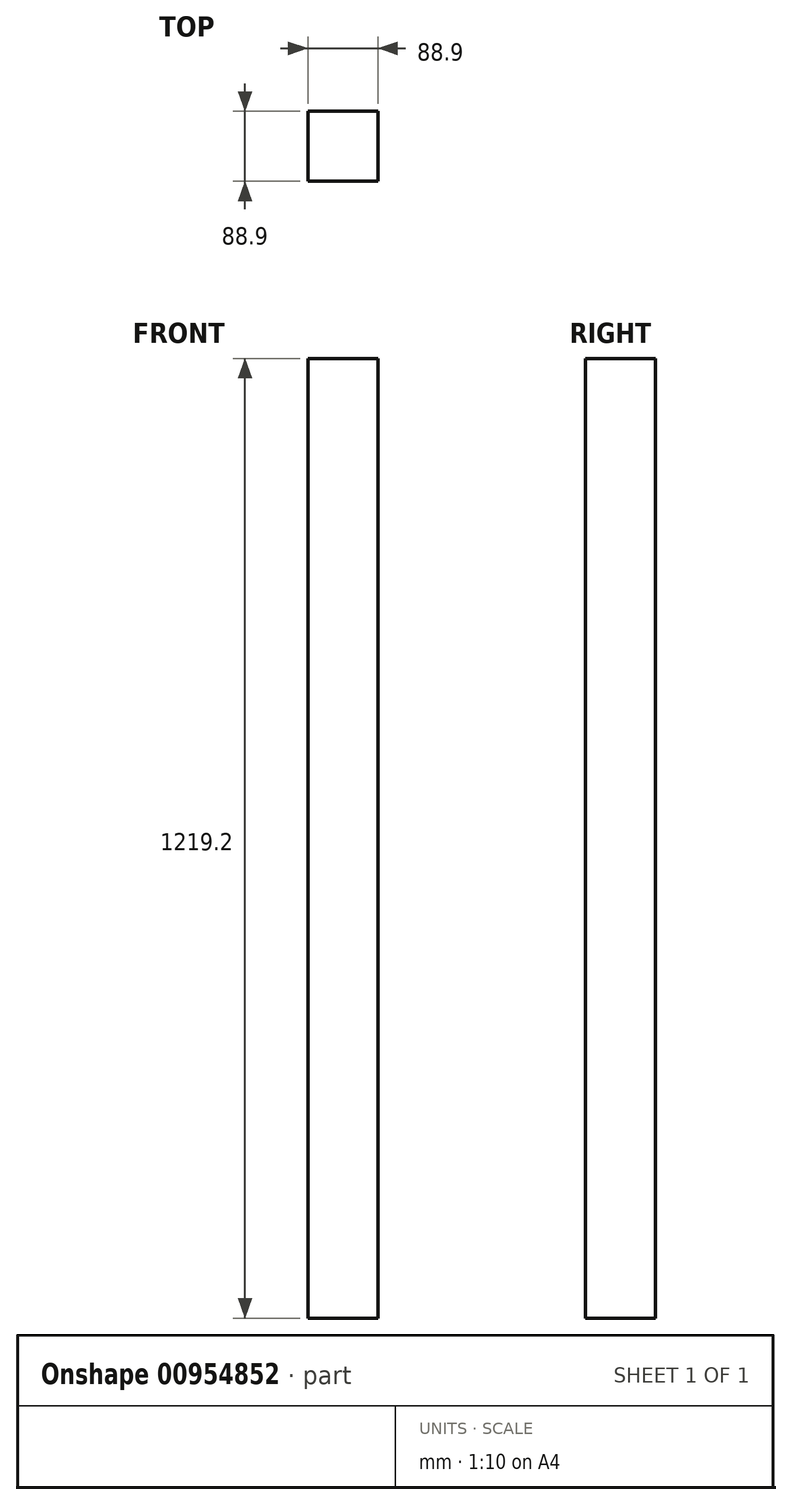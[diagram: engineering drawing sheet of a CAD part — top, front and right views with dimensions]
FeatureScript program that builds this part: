
annotation { "Feature Type Name" : "Feature", "Feature Type Description" : "" }
export const myFeature = defineFeature(function(context is Context, id is Id, definition is map)
    precondition{}
    {
        {
            var Q0;
            Q0=qCreatedBy(makeId("Top.planeOp"),FACE);
            var sketch = newSketch(context, id + "F0", { "sketchPlane" : qUnion([Q0])});
            skLineSegment(sketch, "E0.bottom", {"start": v(-44.45, 44.45) * mm, "end": v(44.45, 44.45) * mm});
            skLineSegment(sketch, "E0.top", {"start": v(-44.45, -44.45) * mm, "end": v(44.45, -44.45) * mm});
            skLineSegment(sketch, "E0.left", {"start": v(-44.45, 44.45) * mm, "end": v(-44.45, -44.45) * mm});
            skLineSegment(sketch, "E0.right", {"start": v(44.45, 44.45) * mm, "end": v(44.45, -44.45) * mm});
            skPoint(sketch, "E1", {"position": v(-44.45, 0) * mm});
            skPoint(sketch, "E2", {"position": v(0, 44.45) * mm});
            skSolve(sketch);
        }
        {
            var Q0;
            Q0=qSketchRegion(id+"F0",true);
            extrude(context, id + "F1", {"entities" : qUnion([Q0]), "depth" : 609.6 * mm, "offsetDistance" : 25.4 * mm, "hasSecondDirection" : true, "secondDirectionOppositeDirection" : true, "secondDirectionDepth" : 609.6 * mm});
        }
    });
